# Revit family: Drabina_ewakuacyjna_standard
name_source: partatom
category: Specialty Equipment
units: mm (PartAtom-declared; Revit-internal decimal feet)

## family parameters
Always vertical = Yes
Cut with Voids When Loaded = No
Host = Wall
Part Type = Normal
Room Calculation Point = No
Round Connector Dimension = Use Diameter
Shared = No

## types (3) — shared parameters
Material = Blacha ocynkowana Ruukki
Type Comments = Drabina z koszem i wejściem na dach
URL = taniedrabiny.pl

## per-type parameters (varying)
| type | Odleglosc_od_sciany | Odsuniecie_od_sciany |
| 16cm od sciany | 160 mm  [stored 0.524934 ft] | 180 mm  [stored 0.590551 ft] |
| 30cm od sciany | 300 mm | 320 mm  [stored 1.04987 ft] |
| 50cm od sciany | 500 mm  [stored 1.64042 ft] | 520 mm  [stored 1.70604 ft] |

note: [stored X ft] marks values corroborated as IEEE doubles in the binary element streams (Revit-internal decimal feet)

## geometry (parser evidence)
native form markers: Blend x6, Sweep x24
no freeform markers — native parametric forms only
